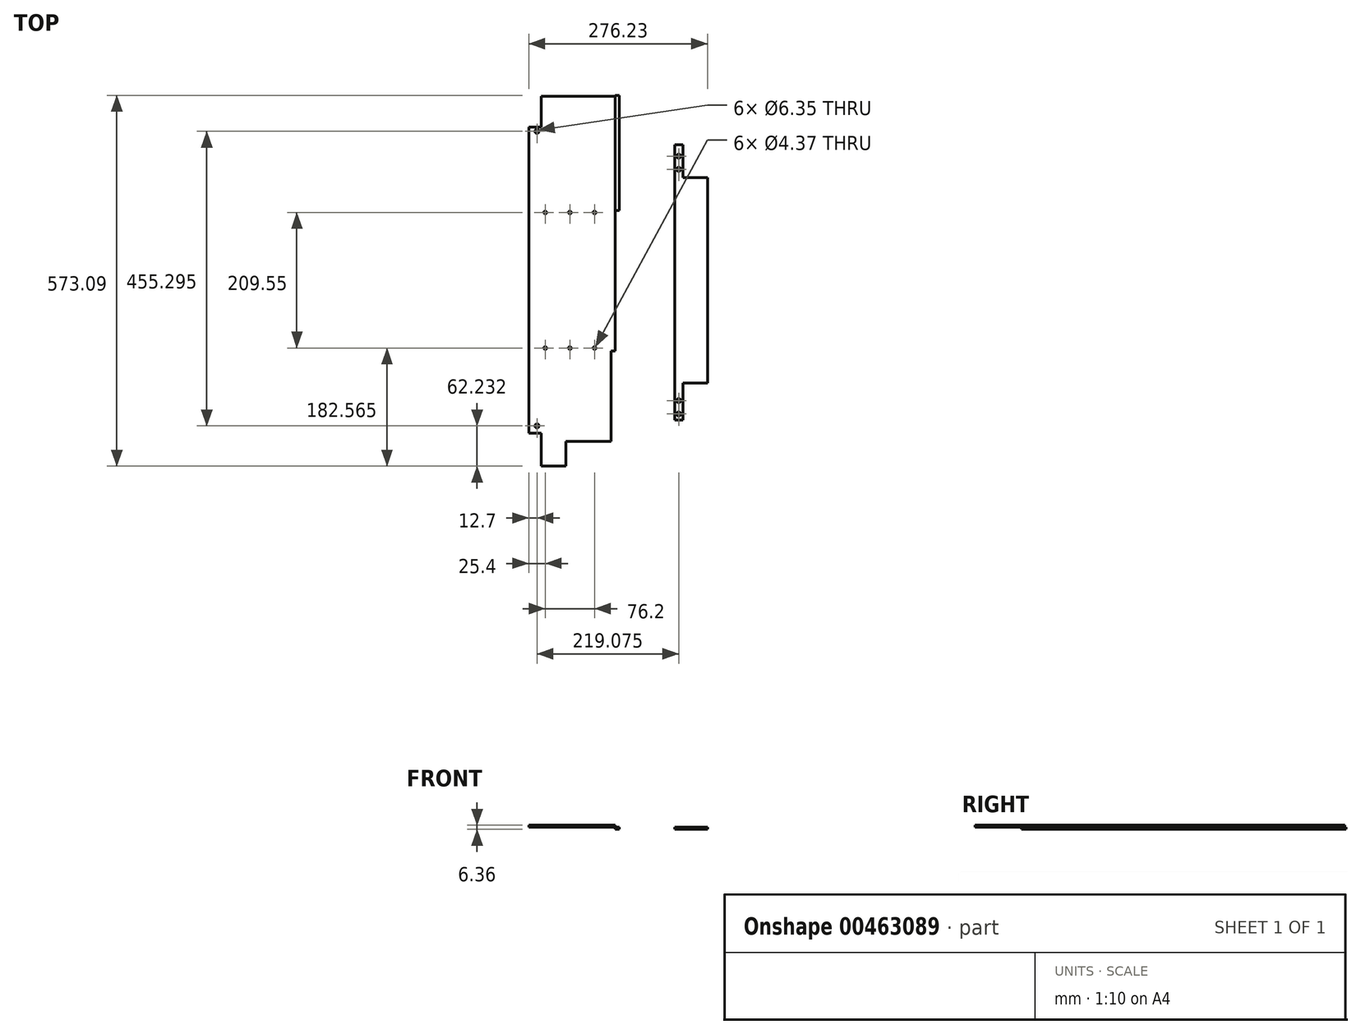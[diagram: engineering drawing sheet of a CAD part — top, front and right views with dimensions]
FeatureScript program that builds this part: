
annotation { "Feature Type Name" : "Feature", "Feature Type Description" : "" }
export const myFeature = defineFeature(function(context is Context, id is Id, definition is map)
    precondition{}
    {
        {
            var Q0;
            Q0=qCreatedBy(makeId("Top.planeOp"),FACE);
            var sketch = newSketch(context, id + "F0", { "sketchPlane" : qUnion([Q0])});
            skLineSegment(sketch, "E0.bottom", {"start": v(-114.3, 284.16) * mm, "end": v(0, 284.16) * mm});
            skLineSegment(sketch, "E0.top", {"start": v(-114.3, -287.34) * mm, "end": v(0, -287.34) * mm});
            skLineSegment(sketch, "E0.left", {"start": v(-114.3, 284.16) * mm, "end": v(-114.3, -287.34) * mm});
            skLineSegment(sketch, "E0.right", {"start": v(0, 284.16) * mm, "end": v(0, -287.34) * mm});
            skLineSegment(sketch, "E1.bottom", {"start": v(-114.3, 236.54) * mm, "end": v(-133.35, 236.54) * mm});
            skLineSegment(sketch, "E1.top", {"start": v(-114.3, -236.54) * mm, "end": v(-133.35, -236.54) * mm});
            skLineSegment(sketch, "E1.left", {"start": v(-114.3, 236.54) * mm, "end": v(-114.3, -236.54) * mm});
            skLineSegment(sketch, "E1.right", {"start": v(-133.35, 236.54) * mm, "end": v(-133.35, -236.54) * mm});
            skLineSegment(sketch, "E2", {"start": v(-133.35, -104.78) * mm, "end": v(0, -104.78) * mm, "construction": true});
            skCircle(sketch, "E3", {"center": v(-31.75, -104.78) * mm, "radius": 2.18 * mm});
            skLineSegment(sketch, "E4", {"start": v(-114.3, 0) * mm, "end": v(0, 0) * mm, "construction": true});
            skLineSegment(sketch, "E5.bottom", {"start": v(0, -287.34) * mm, "end": v(-6.35, -287.34) * mm});
            skLineSegment(sketch, "E5.top", {"start": v(0, -109.54) * mm, "end": v(-6.35, -109.54) * mm});
            skLineSegment(sketch, "E5.left", {"start": v(0, -287.34) * mm, "end": v(0, -109.54) * mm});
            skLineSegment(sketch, "E5.right", {"start": v(-6.35, -287.34) * mm, "end": v(-6.35, -109.54) * mm});
            skCircle(sketch, "E6", {"center": v(-69.85, -104.78) * mm, "radius": 2.18 * mm});
            skCircle(sketch, "E7", {"center": v(-107.95, -104.78) * mm, "radius": 2.18 * mm});
            skPoint(sketch, "E8.endSnap0", {"position": v(-57.15, -287.34) * mm});
            skLineSegment(sketch, "E9.bottom", {"start": v(0, -287.34) * mm, "end": v(-76.2, -287.34) * mm});
            skLineSegment(sketch, "E9.top", {"start": v(0, -249.24) * mm, "end": v(-76.2, -249.24) * mm});
            skLineSegment(sketch, "E9.left", {"start": v(0, -287.34) * mm, "end": v(0, -249.24) * mm});
            skLineSegment(sketch, "E9.right", {"start": v(-76.2, -287.34) * mm, "end": v(-76.2, -249.24) * mm});
            skCircle(sketch, "E10", {"center": v(-120.65, 230.19) * mm, "radius": 3.18 * mm});
            skCircle(sketch, "E11", {"center": v(-120.65, -225.1) * mm, "radius": 3.18 * mm});
            skLineSegment(sketch, "E12", {"start": v(-120.65, -236.54) * mm, "end": v(-120.65, 236.54) * mm, "construction": true});
            skCircle(sketch, "E13.MirrorC", {"center": v(-107.95, 104.77) * mm, "radius": 2.18 * mm});
            skCircle(sketch, "E14.MirrorC", {"center": v(-69.85, 104.77) * mm, "radius": 2.18 * mm});
            skCircle(sketch, "E15.MirrorC", {"center": v(-31.75, 104.78) * mm, "radius": 2.18 * mm});
            skPoint(sketch, "E16.endSnap0", {"position": v(-133.35, 0) * mm});
            skSolve(sketch);
        }
        {
            var Q0;
            {var subQ2=sQuery(id+"F0.wireOp",EDGE,"E0.bottom");Q0=makeQuery(id+"F0.imprint","IMPRINT",FACE,{"disambiguationData":[TD([[makeQuery(id+"F0.imprint","IMPRINT",EDGE,{"derivedFrom":subQ2}),-1.0]])]});}
            var Q1;
            Q1=makeQuery(id+"F0.imprint","IMPRINT",FACE,{"disambiguationData":[TD([[makeQuery(id+"F0.imprint","IMPRINT",EDGE,{"derivedFrom":sQuery(id+"F0.wireOp",EDGE,"E1.bottom")}),1.0]])]});
            var Q2;
            {var subQ0=sQuery(id+"F0.wireOp",EDGE,"C9tF2391-lg0z-U8Q0-cbS7-5h3BA2hwrsg4.bottom");Q2=makeQuery(id+"F0.imprint","IMPRINT",FACE,{"disambiguationData":[TD([[makeQuery(id+"F0.imprint","IMPRINT",EDGE,{"derivedFrom":subQ0}),1.0]])]});}
            var Q3;
            {var subQ0=sQuery(id+"F0.wireOp",EDGE,"C9tF2391-lg0z-U8Q0-cbS7-5h3BA2hwrsg4.top");Q3=makeQuery(id+"F0.imprint","IMPRINT",FACE,{"disambiguationData":[TD([[makeQuery(id+"F0.imprint","IMPRINT",EDGE,{"derivedFrom":subQ0}),-1.0]])]});}
            var Q4;
            {var subQ1=sQuery(id+"F0.wireOp",EDGE,"E1.top");Q4=makeQuery(id+"F0.imprint","IMPRINT",FACE,{"disambiguationData":[TD([[makeQuery(id+"F0.imprint","IMPRINT",EDGE,{"derivedFrom":subQ1}),-1.0]])]});}
            extrude(context, id + "F1", {"entities" : qUnion([Q0, Q1, Q2, Q3, Q4]), "depth" : 3.17 * mm, "offsetDistance" : 25.4 * mm});
        }
        {
            var Q0;
            Q0=makeQuery(id+"F1.opExtrude","CAP_FACE",FACE,{"disambiguationData":[OSD([sQuery(id+"F0.wireOp",EDGE,"E0.bottom"),sQuery(id+"F0.wireOp",EDGE,"E0.top"),sQuery(id+"F0.wireOp",EDGE,"E0.left"),sQuery(id+"F0.wireOp",EDGE,"E0.right"),sQuery(id+"F0.wireOp",EDGE,"E1.bottom"),sQuery(id+"F0.wireOp",EDGE,"E1.top"),sQuery(id+"F0.wireOp",EDGE,"E1.right"),sQuery(id+"F0.wireOp",EDGE,"cqP3jTrP-MJX9-YQpH-X3wt-yMHeYC4tcMe0.top"),sQuery(id+"F0.wireOp",EDGE,"cqP3jTrP-MJX9-YQpH-X3wt-yMHeYC4tcMe0.right"),sQuery(id+"F0.wireOp",EDGE,"E3"),sQuery(id+"F0.wireOp",EDGE,"N4cTxHvr-xVKP-zUrY-svA7-J4Bx8T6q11gZ"),sQuery(id+"F0.wireOp",EDGE,"2UR2iMdC-GheW-WnGl-vyb2-4ksJVWEQtWx0"),sQuery(id+"F0.wireOp",EDGE,"883aba63-0116-4ce9-921b-836c0d46251e0.MirrorC"),sQuery(id+"F0.wireOp",EDGE,"6b6388c8-aac4-4146-a75b-c18c396dbd7b0.MirrorC"),sQuery(id+"F0.wireOp",EDGE,"5b3af853-fe57-4a35-8c14-3b93798950fc0.MirrorC")])],"isStart":true});
            var sketch = newSketch(context, id + "F2", { "sketchPlane" : qUnion([Q0])});
            skLineSegment(sketch, "E17.bottom", {"start": v(0, -285.75) * mm, "end": v(92.07, -285.75) * mm});
            skLineSegment(sketch, "E17.top", {"start": v(0, 285.75) * mm, "end": v(92.07, 285.75) * mm});
            skLineSegment(sketch, "E17.left", {"start": v(0, -285.75) * mm, "end": v(0, 285.75) * mm});
            skLineSegment(sketch, "E17.right", {"start": v(92.08, -285.75) * mm, "end": v(92.07, 285.75) * mm});
            skLineSegment(sketch, "E18.bottom", {"start": v(92.07, -209.55) * mm, "end": v(104.78, -209.55) * mm});
            skLineSegment(sketch, "E18.top", {"start": v(92.07, 215.9) * mm, "end": v(104.77, 215.9) * mm});
            skLineSegment(sketch, "E18.left", {"start": v(92.08, -209.55) * mm, "end": v(92.07, 215.9) * mm});
            skLineSegment(sketch, "E18.right", {"start": v(104.78, -209.55) * mm, "end": v(104.77, 215.9) * mm});
            skLineSegment(sketch, "E19", {"start": v(0, 104.78) * mm, "end": v(92.07, 104.78) * mm, "construction": true});
            skLineSegment(sketch, "E20", {"start": v(0, 0) * mm, "end": v(92.08, 0) * mm, "construction": true});
            skCircle(sketch, "E21", {"center": v(19.05, 104.78) * mm, "radius": 2.18 * mm});
            skCircle(sketch, "E22", {"center": v(57.15, 104.78) * mm, "radius": 2.18 * mm});
            skCircle(sketch, "E23", {"center": v(82.55, 104.78) * mm, "radius": 2.18 * mm});
            skLineSegment(sketch, "E24.bottom", {"start": v(0, -285.75) * mm, "end": v(6.35, -285.75) * mm});
            skLineSegment(sketch, "E24.top", {"start": v(0, -107.95) * mm, "end": v(6.35, -107.95) * mm});
            skLineSegment(sketch, "E24.left", {"start": v(0, -285.75) * mm, "end": v(0, -107.95) * mm});
            skLineSegment(sketch, "E24.right", {"start": v(6.35, -285.75) * mm, "end": v(6.35, -107.95) * mm});
            skLineSegment(sketch, "E25", {"start": v(0, 260.35) * mm, "end": v(25.4, 285.75) * mm});
            skCircle(sketch, "E26", {"center": v(98.42, 206.63) * mm, "radius": 3.18 * mm});
            skCircle(sketch, "E27", {"center": v(98.42, 186.06) * mm, "radius": 3.18 * mm});
            skCircle(sketch, "E28", {"center": v(98.43, -191.77) * mm, "radius": 3.18 * mm});
            skCircle(sketch, "E29", {"center": v(98.43, -171.45) * mm, "radius": 3.18 * mm});
            skLineSegment(sketch, "E30", {"start": v(98.43, -209.55) * mm, "end": v(98.42, 215.9) * mm, "construction": true});
            skCircle(sketch, "E31.MirrorC", {"center": v(22.23, -104.78) * mm, "radius": 2.18 * mm});
            skCircle(sketch, "E32.MirrorC", {"center": v(60.33, -104.78) * mm, "radius": 2.18 * mm});
            skCircle(sketch, "E33.MirrorC", {"center": v(85.73, -104.78) * mm, "radius": 2.18 * mm});
            skLineSegment(sketch, "E34", {"start": v(104.78, -104.78) * mm, "end": v(0, -104.78) * mm, "construction": true});
            skLineSegment(sketch, "E35.bottom", {"start": v(104.78, -158.75) * mm, "end": v(142.88, -158.75) * mm});
            skLineSegment(sketch, "E35.top", {"start": v(104.78, 158.75) * mm, "end": v(142.88, 158.75) * mm});
            skLineSegment(sketch, "E35.left", {"start": v(104.78, -158.75) * mm, "end": v(104.78, 158.75) * mm});
            skLineSegment(sketch, "E35.right", {"start": v(142.88, -158.75) * mm, "end": v(142.87, 158.75) * mm});
            skLineSegment(sketch, "E36", {"start": v(92.08, 0) * mm, "end": v(142.88, 0) * mm});
            skSolve(sketch);
        }
        {
            var Q0;
            {var subQ3=sQuery(id+"F2.wireOp",EDGE,"E17.bottom");Q0=makeQuery(id+"F2.imprint","IMPRINT",FACE,{"disambiguationData":[TD([[makeQuery(id+"F2.imprint","IMPRINT",EDGE,{"derivedFrom":subQ3}),1.0]])]});}
            var Q1;
            Q1=makeQuery(id+"F2.imprint","IMPRINT",FACE,{"disambiguationData":[TD([[makeQuery(id+"F2.imprint","IMPRINT",EDGE,{"derivedFrom":sQuery(id+"F2.wireOp",EDGE,"E18.bottom")}),1.0]])]});
            var Q2;
            {var subQ1=sQuery(id+"F2.wireOp",EDGE,"E18.top");Q2=makeQuery(id+"F2.imprint","IMPRINT",FACE,{"disambiguationData":[TD([[makeQuery(id+"F2.imprint","IMPRINT",EDGE,{"derivedFrom":subQ1}),-1.0]])]});}
            var Q3;
            {var subQ0=sQuery(id+"F2.wireOp",EDGE,"E35.bottom");Q3=makeQuery(id+"F2.imprint","IMPRINT",FACE,{"disambiguationData":[TD([[makeQuery(id+"F2.imprint","IMPRINT",EDGE,{"derivedFrom":subQ0}),1.0]])]});}
            var Q4;
            {var subQ0=sQuery(id+"F2.wireOp",EDGE,"E35.top");Q4=makeQuery(id+"F2.imprint","IMPRINT",FACE,{"disambiguationData":[TD([[makeQuery(id+"F2.imprint","IMPRINT",EDGE,{"derivedFrom":subQ0}),-1.0]])]});}
            extrude(context, id + "F3", {"entities" : qUnion([Q0, Q1, Q2, Q3, Q4]), "depth" : 3.17 * mm, "offsetDistance" : 25.4 * mm});
        }
    });
